# Revit family: FU_Inspec_Area_6-1
name_source: partatom
category: Furniture
units: mm (PartAtom-declared; Revit-internal decimal feet)

## family parameters
Always vertical = Yes
Cut with Voids When Loaded = No
OmniClass Number = 23.40.20.00
OmniClass Title = General Furniture and Specialties
Room Calculation Point = No
Shared = No
Work Plane-Based = No

## types (4) — shared parameters
Assembly Code = E2020
Description = Upholstered easy chair with powder coated or chromium plated cast aluminium sled base, and shell of fibre board with highly resilient polyurethane foam.
Keynote = 46.B
Legs Material = Metal - Chrome - Polished
Manufacturer = Inspec
Model = area 6.1
URL = https://inspecfurniture.com
zero-valued in all types: Default Elevation

## per-type parameters (varying)
| type | Seat Material |
| Fabric - Grey | Fabric - Grey |
| Fabric - Red | Fabric - Red |
| Fabric - Yellow | Fabric - Yellow - Bright |
| Fabric - Beige | Fabric - Beige |

## geometry (parser evidence)
native form markers: Blend x14, Sweep x5
no freeform markers — native parametric forms only
